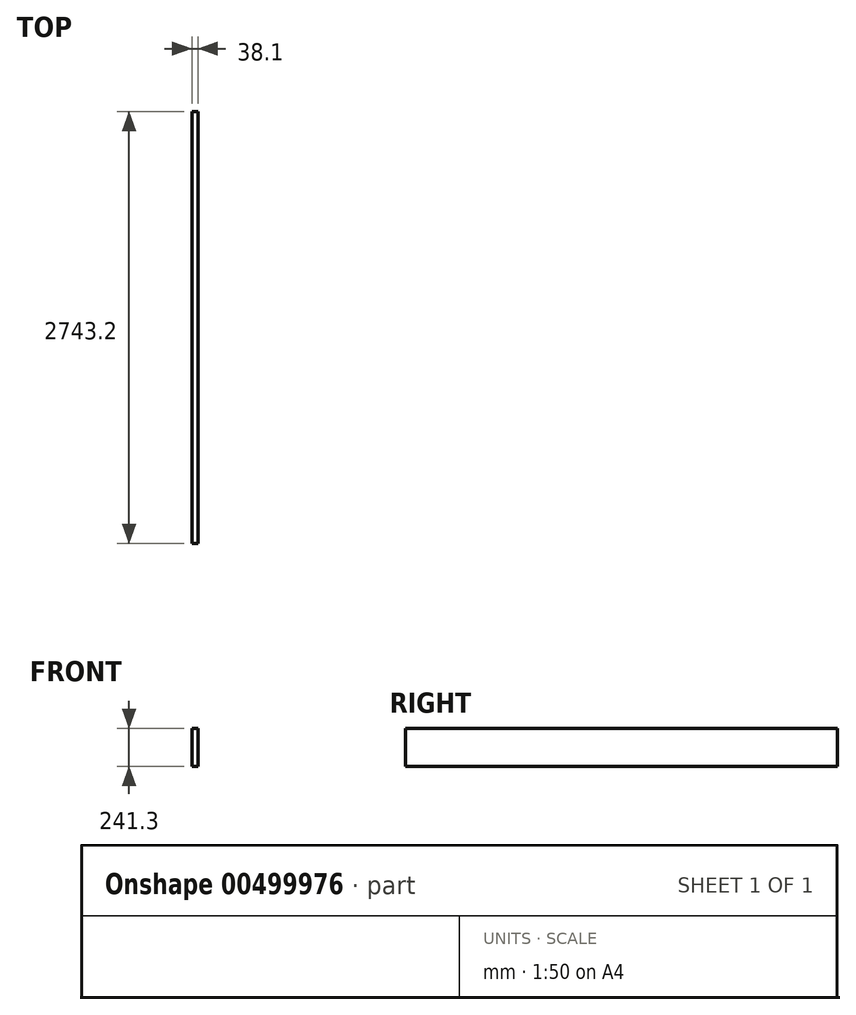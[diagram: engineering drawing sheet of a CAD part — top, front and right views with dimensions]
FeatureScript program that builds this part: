
annotation { "Feature Type Name" : "Feature", "Feature Type Description" : "" }
export const myFeature = defineFeature(function(context is Context, id is Id, definition is map)
    precondition{}
    {
        {
            var Q0;
            Q0=qCreatedBy(makeId("Right.planeOp"),FACE);
            var sketch = newSketch(context, id + "F0", { "sketchPlane" : qUnion([Q0])});
            skLineSegment(sketch, "E0.bottom", {"start": v(-1371.6, 120.65) * mm, "end": v(1371.6, 120.65) * mm});
            skLineSegment(sketch, "E0.top", {"start": v(-1371.6, -120.65) * mm, "end": v(1371.6, -120.65) * mm});
            skLineSegment(sketch, "E0.left", {"start": v(-1371.6, 120.65) * mm, "end": v(-1371.6, -120.65) * mm});
            skLineSegment(sketch, "E0.right", {"start": v(1371.6, 120.65) * mm, "end": v(1371.6, -120.65) * mm});
            skPoint(sketch, "E0.middle", {"position": v(0, 0) * mm});
            skSolve(sketch);
        }
        {
            var Q0;
            Q0 = qSketchRegion(id + "F0", true);
            extrude(context, id + "F1", {"entities" : qUnion([Q0]), "depth" : 38.1 * mm, "offsetDistance" : 25.4 * mm});
        }
    });
